# Revit family: QSC CXD 8 Channel Amplifier
name_source: partatom
category: Generic Models
revit_build: Autodesk Revit 2014 (Build: 20130308_1515(x64)
units: mm (PartAtom-declared; Revit-internal decimal feet)

## types (4) — shared parameters
Depth = 434 mm  [stored 1.42388 ft]
Height = 88.9 mm  [stored 0.291667 ft]
Manufacturer = QSC
Manufacturer URL = http://www.qsc.com
Product Documentation Link = https://www.qsc.com
Regulatory Compliance = UL, CE, RoHS/WEEE, FCC Class A
Voltage AC = 100-240 at 50-60 Hz
Width = 482.6 mm  [stored 1.58333 ft]
zero-valued in all types: Default Elevation

## per-type parameters (varying)
| type | Description | Product Page URL | Weight Dimensional (kg) | Weight Dimensional (lb) | Weight Product (kg) | Weight Product (lb) |
| CXD8.4Q | 4000 Watt Multi-Channel Network Amplifier | https://www.qsc.com | 13.2 | 29 | 11.3 | 25 |
| CXD8.4Qn | 4000 Watt Multi-Channel Network Only Amplifier | https://www.qsc.com
https://www.qsc.com
https://www.qsc.com | 13.2 | 29 | 11.3 | 25 |
| CXD8.8Q | 8000 Watt Multi-Channel Network Amplifier | https://www.qsc.com | 13.6 | 30 | 11.8 | 26 |
| CXD8.8Qn | 8000 Watt Multi-Channel Network Only Amplifier | https://www.qsc.com | 13.6 | 30 | 11.8 | 26 |

note: column(s) folded — value = type name in every type: Model

note: [stored X ft] marks values corroborated as IEEE doubles in the binary element streams (Revit-internal decimal feet)

## geometry (parser evidence)
native form markers: Blend x4, Sweep x9
no freeform markers — native parametric forms only
